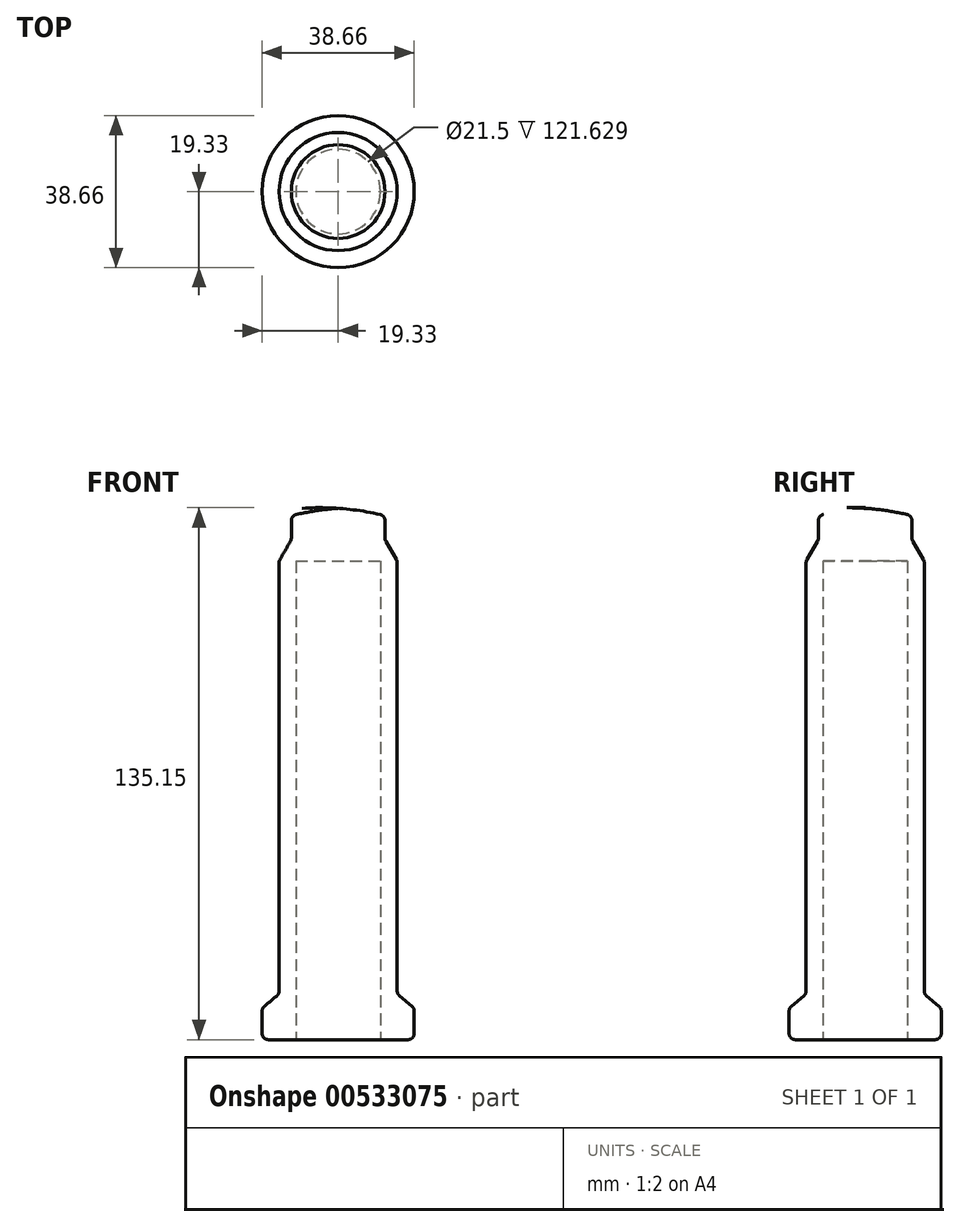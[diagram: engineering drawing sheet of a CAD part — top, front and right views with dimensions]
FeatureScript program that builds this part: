
annotation { "Feature Type Name" : "Feature", "Feature Type Description" : "" }
export const myFeature = defineFeature(function(context is Context, id is Id, definition is map)
    precondition{}
    {
        {
            var Q0;
            Q0=qCreatedBy(makeId("Front.planeOp"),FACE);
            var sketch = newSketch(context, id + "F0", { "sketchPlane" : qUnion([Q0])});
            skLineSegment(sketch, "E0", {"start": v(0, 135) * mm, "end": v(0, 121.63) * mm});
            skLineSegment(sketch, "E1", {"start": v(0, 121.63) * mm, "end": v(10.75, 121.63) * mm});
            skLineSegment(sketch, "E2", {"start": v(10.75, 121.63) * mm, "end": v(10.75, 0) * mm});
            skLineSegment(sketch, "E3", {"start": v(10.75, 0) * mm, "end": v(19.32, 0) * mm});
            skLineSegment(sketch, "E4", {"start": v(19.32, 0) * mm, "end": v(19.32, 8) * mm});
            skLineSegment(sketch, "E5", {"start": v(19.32, 8) * mm, "end": v(15, 11.63) * mm});
            skLineSegment(sketch, "E6", {"start": v(15, 11.63) * mm, "end": v(15, 121.63) * mm});
            skLineSegment(sketch, "E7", {"start": v(11.9, 127) * mm, "end": v(15, 121.63) * mm});
            skLineSegment(sketch, "E8", {"start": v(11.9, 127) * mm, "end": v(11.9, 133.13) * mm});
            skLineSegment(sketch, "E9", {"start": v(0, 0) * mm, "end": v(0, 135) * mm, "construction": true});
            skArc(sketch, "E10", {"start": v(11.9, 133.13) * mm, "mid": v(6, 134.33) * mm, "end": v(0, 135) * mm});
            skSolve(sketch);
        }
        {
            var Q0;
            Q0 = qSketchRegion(id + "F0", true);
            var Q1;
            Q1=sQuery(id+"F0.wireOp",EDGE,"E9");
            revolve(context, id + "F1", {"surfaceOperationType" : NewSurfaceOperationType.NEW, "entities" : qUnion([Q0]), "axis" : qUnion([Q1]), "revolveType" : RevolveType.FULL});
        }
        {
            var Q0;
            Q0=makeQuery(id+"F1.opRevolve","SWEPT_EDGE",EDGE,{"disambiguationData":[OSD([sQuery(id+"F0.wireOp",EDGE,"E8"),sQuery(id+"F0.wireOp",EDGE,"E10")])]});
            var Q1;
            Q1=makeQuery(id+"F1.opRevolve","SWEPT_EDGE",EDGE,{"disambiguationData":[OSD([sQuery(id+"F0.wireOp",EDGE,"E7"),sQuery(id+"F0.wireOp",EDGE,"E8")])]});
            var Q2;
            Q2=makeQuery(id+"F1.opRevolve","SWEPT_EDGE",EDGE,{"disambiguationData":[OSD([sQuery(id+"F0.wireOp",EDGE,"E6"),sQuery(id+"F0.wireOp",EDGE,"E7")])]});
            var Q3;
            Q3=makeQuery(id+"F1.opRevolve","SWEPT_EDGE",EDGE,{"disambiguationData":[OSD([sQuery(id+"F0.wireOp",EDGE,"E5"),sQuery(id+"F0.wireOp",EDGE,"E6")])]});
            var Q4;
            Q4=makeQuery(id+"F1.opRevolve","SWEPT_EDGE",EDGE,{"disambiguationData":[OSD([sQuery(id+"F0.wireOp",EDGE,"E4"),sQuery(id+"F0.wireOp",EDGE,"E5")])]});
            var Q5;
            Q5=makeQuery(id+"F1.opRevolve","SWEPT_EDGE",EDGE,{"disambiguationData":[OSD([sQuery(id+"F0.wireOp",EDGE,"E3"),sQuery(id+"F0.wireOp",EDGE,"E4")])]});
            fillet(context, id + "F2", {"entities" : qUnion([Q0, Q1, Q2, Q3, Q4, Q5]), "radius" : 1.6 * mm, "tangentPropagation" : true, "allowEdgeOverflow" : false});
        }
        {
            var Q0;
            Q0=qCreatedBy(makeId("Right.planeOp"),FACE);
            cPlane(context, id + "F3", {"entities" : qUnion([Q0]), "cplaneType" : CPlaneType.OFFSET, "offset" : 20 * mm, "width" : 150 * mm, "height" : 150 * mm});
        }
    });
